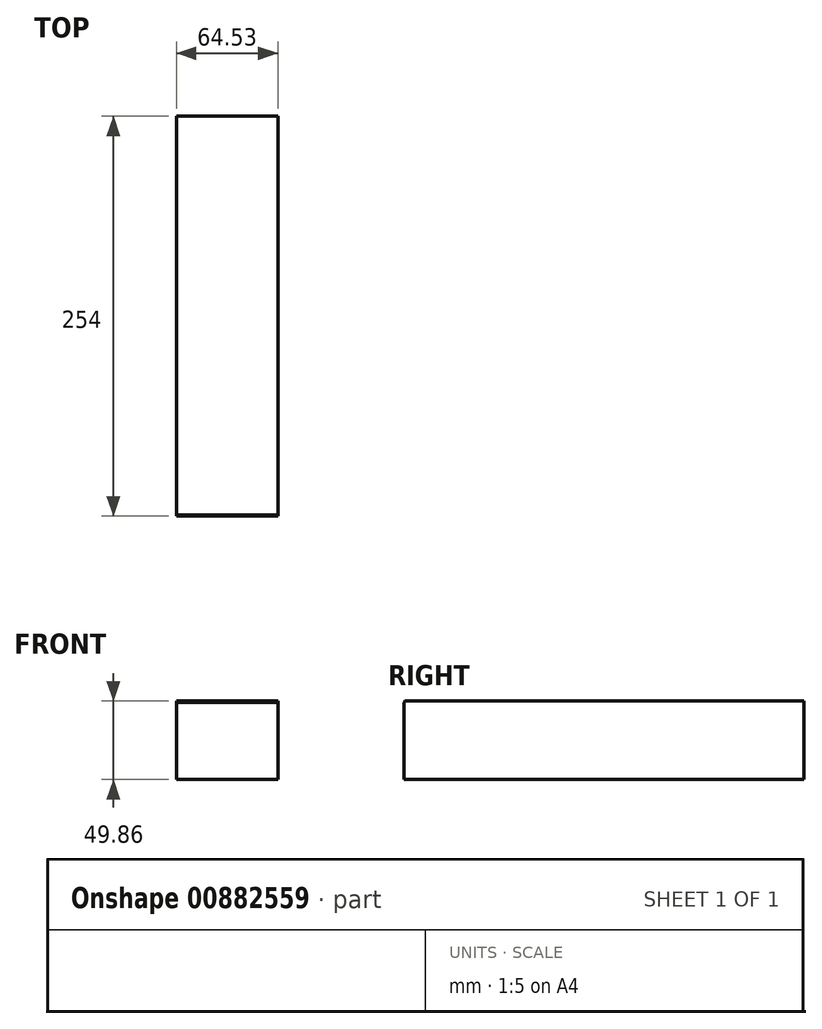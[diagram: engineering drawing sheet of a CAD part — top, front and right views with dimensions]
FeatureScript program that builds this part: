
annotation { "Feature Type Name" : "Feature", "Feature Type Description" : "" }
export const myFeature = defineFeature(function(context is Context, id is Id, definition is map)
    precondition{}
    {
        {
            var Q0;
            Q0=qCreatedBy(makeId("Front.planeOp"),FACE);
            var sketch = newSketch(context, id + "F0", { "sketchPlane" : qUnion([Q0])});
            skLineSegment(sketch, "E0.bottom", {"start": v(-64.53, 49.86) * mm, "end": v(0, 49.86) * mm});
            skLineSegment(sketch, "E0.top", {"start": v(-64.53, 0) * mm, "end": v(0, 0) * mm});
            skLineSegment(sketch, "E0.left", {"start": v(-64.53, 49.86) * mm, "end": v(-64.53, 0) * mm});
            skLineSegment(sketch, "E0.right", {"start": v(0, 49.86) * mm, "end": v(0, 0) * mm});
            skSolve(sketch);
        }
        {
            var Q0;
            Q0=qSketchRegion(id+"F0",true);
            extrude(context, id + "F1", {"entities" : qUnion([Q0]), "depth" : 127 * mm, "offsetDistance" : 25.4 * mm, "hasSecondDirection" : true, "secondDirectionOppositeDirection" : true, "secondDirectionDepth" : 127 * mm});
        }
        {
            var Q0;
            Q0=makeQuery(id+"F1.opExtrude","CAP_FACE",FACE,{"disambiguationData":[OSD([sQuery(id+"F0.wireOp",EDGE,"E0.bottom"),sQuery(id+"F0.wireOp",EDGE,"E0.top"),sQuery(id+"F0.wireOp",EDGE,"E0.left"),sQuery(id+"F0.wireOp",EDGE,"E0.right")])],"isStart":false});
            var sketch = newSketch(context, id + "F2", { "sketchPlane" : qUnion([Q0])});
            skCircle(sketch, "E1", {"center": v(-34.08, 24.93) * mm, "radius": 15.41 * mm});
            skPoint(sketch, "E1.centerSnap0", {"position": v(-64.53, 24.93) * mm});
            skSolve(sketch);
        }
        {
            var Q0;
            Q0=makeQuery(id+"F1.opExtrude","CAP_EDGE",EDGE,{"disambiguationData":[OSD([sQuery(id+"F0.wireOp",EDGE,"E0.bottom")])],"isStart":false});
            chamfer(context, id + "F3", {"entities" : qUnion([Q0]), "width" : 0.76 * mm, "tangentPropagation" : true});
        }
    });
